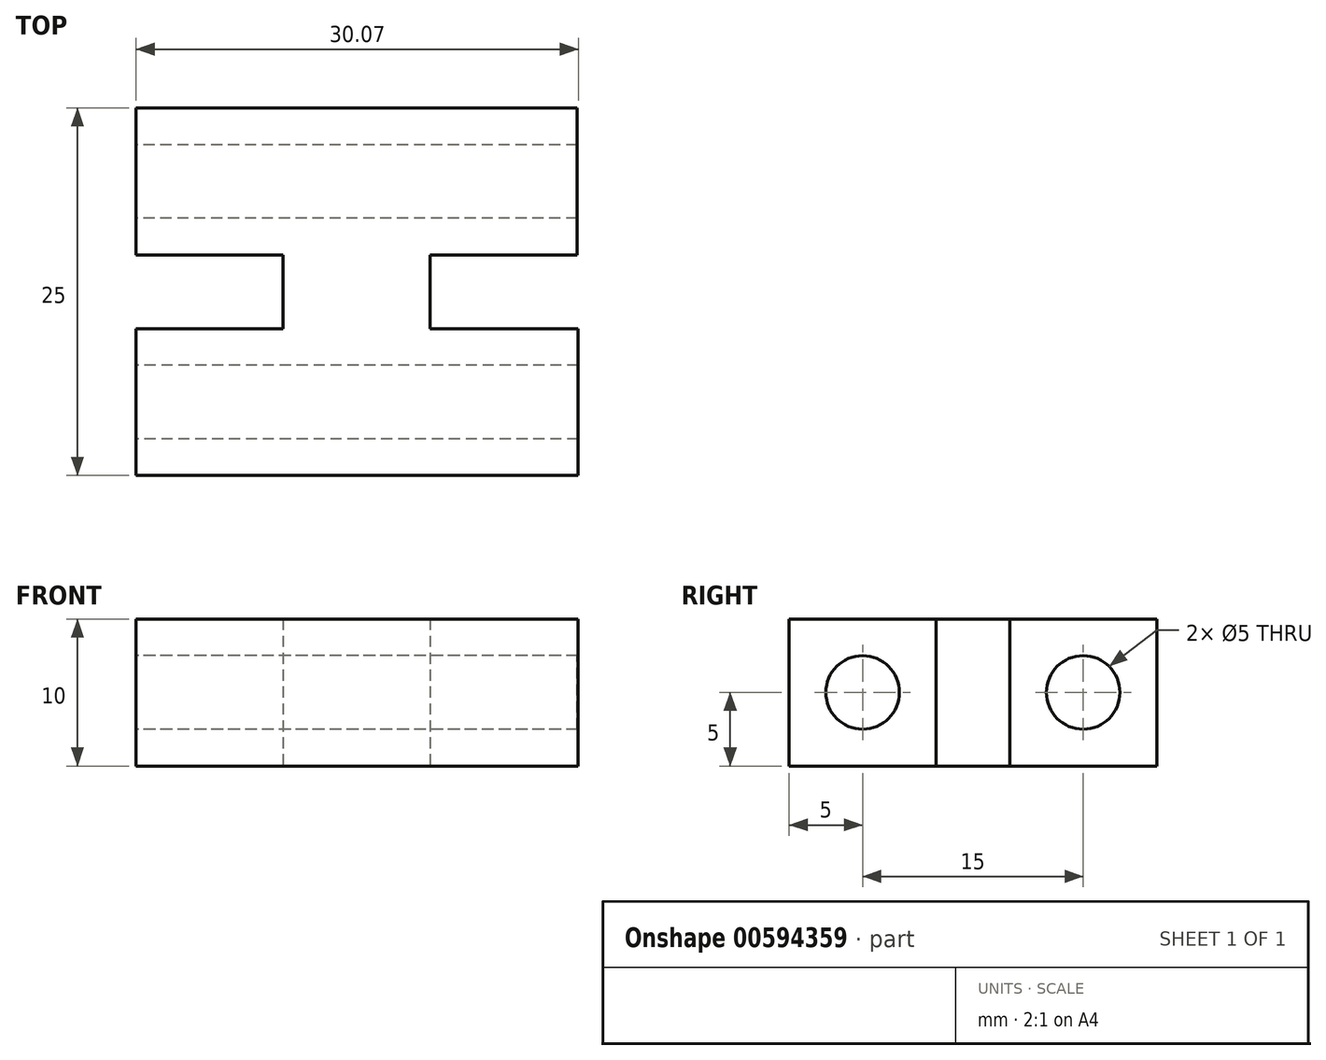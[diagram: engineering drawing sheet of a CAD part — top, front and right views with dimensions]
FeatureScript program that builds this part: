
annotation { "Feature Type Name" : "Feature", "Feature Type Description" : "" }
export const myFeature = defineFeature(function(context is Context, id is Id, definition is map)
    precondition{}
    {
        {
            var Q0;
            Q0=qCreatedBy(makeId("Top.planeOp"),FACE);
            var sketch = newSketch(context, id + "F0", { "sketchPlane" : qUnion([Q0])});
            skLineSegment(sketch, "E0", {"start": v(0, 0) * mm, "end": v(30, 0) * mm});
            skLineSegment(sketch, "E1", {"start": v(30, 0) * mm, "end": v(30, -10) * mm});
            skLineSegment(sketch, "E2", {"start": v(30, -10) * mm, "end": v(20, -10) * mm});
            skLineSegment(sketch, "E3", {"start": v(20, -10) * mm, "end": v(20, -15) * mm});
            skLineSegment(sketch, "E4", {"start": v(20, -15) * mm, "end": v(30.07, -15) * mm});
            skLineSegment(sketch, "E5", {"start": v(30.07, -15) * mm, "end": v(30.07, -25) * mm});
            skLineSegment(sketch, "E6", {"start": v(30.07, -25) * mm, "end": v(0, -25) * mm});
            skLineSegment(sketch, "E7", {"start": v(0, -25) * mm, "end": v(0, -15) * mm});
            skLineSegment(sketch, "E8", {"start": v(0, -15) * mm, "end": v(10, -15) * mm});
            skLineSegment(sketch, "E9", {"start": v(10, -15) * mm, "end": v(10, -10) * mm});
            skLineSegment(sketch, "E10", {"start": v(10, -10) * mm, "end": v(0, -10) * mm});
            skLineSegment(sketch, "E11", {"start": v(0, -10) * mm, "end": v(0, 0) * mm});
            skSolve(sketch);
        }
        {
            var Q0;
            Q0=qSketchRegion(id+"F0",true);
            extrude(context, id + "F1", {"entities" : qUnion([Q0]), "depth" : 10 * mm, "offsetDistance" : 25 * mm});
        }
        {
            var Q0;
            Q0=makeQuery(id+"F1.opExtrude","SWEPT_FACE",FACE,{"disambiguationData":[OSD([sQuery(id+"F0.wireOp",EDGE,"E11")])]});
            cPlane(context, id + "F2", {"entities" : qUnion([Q0]), "cplaneType" : CPlaneType.OFFSET, "offset" : 0 * mm, "width" : 150 * mm, "height" : 150 * mm});
        }
        {
            var Q0;
            Q0=qCreatedBy(id+"F2.planeOp",FACE);
            var sketch = newSketch(context, id + "F3", { "sketchPlane" : qUnion([Q0])});
            skCircle(sketch, "E12", {"center": v(5, 5) * mm, "radius": 2.5 * mm});
            skCircle(sketch, "E13", {"center": v(20, 5) * mm, "radius": 2.5 * mm});
            skSolve(sketch);
        }
        {
            var Q0;
            Q0=qSketchRegion(id+"F3",true);
            extrude(context, id + "F4", {"entities" : qUnion([Q0]), "operationType" : NewBodyOperationType.REMOVE, "oppositeDirection" : true, "depth" : 45.9 * mm, "offsetDistance" : 25 * mm});
        }
    });
